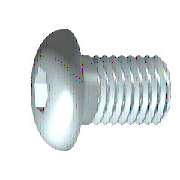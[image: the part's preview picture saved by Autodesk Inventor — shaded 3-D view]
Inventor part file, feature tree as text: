
AUTODESK INVENTOR PART (.ipt)
format: ipt  version: 2024.1 (Build 281209000, 209)  size: 197,120 bytes
history: native  units: mm (DEFAULTED — no unit token found)
features: extrude x1, plane x1, fillet x1
ambient origin geometry x7: Origin, YZ Plane, XY Plane, X Axis, Y Axis, Z Axis, Center Point
bodies: Solid1 (feature_tree), Body (feature_tree)
feature tree (3):
  extrude  "Slot"  Depth=6.5mm
  plane  "Work Plane1"
  fillet  "Fillet2"  Radius=0.306825mm
